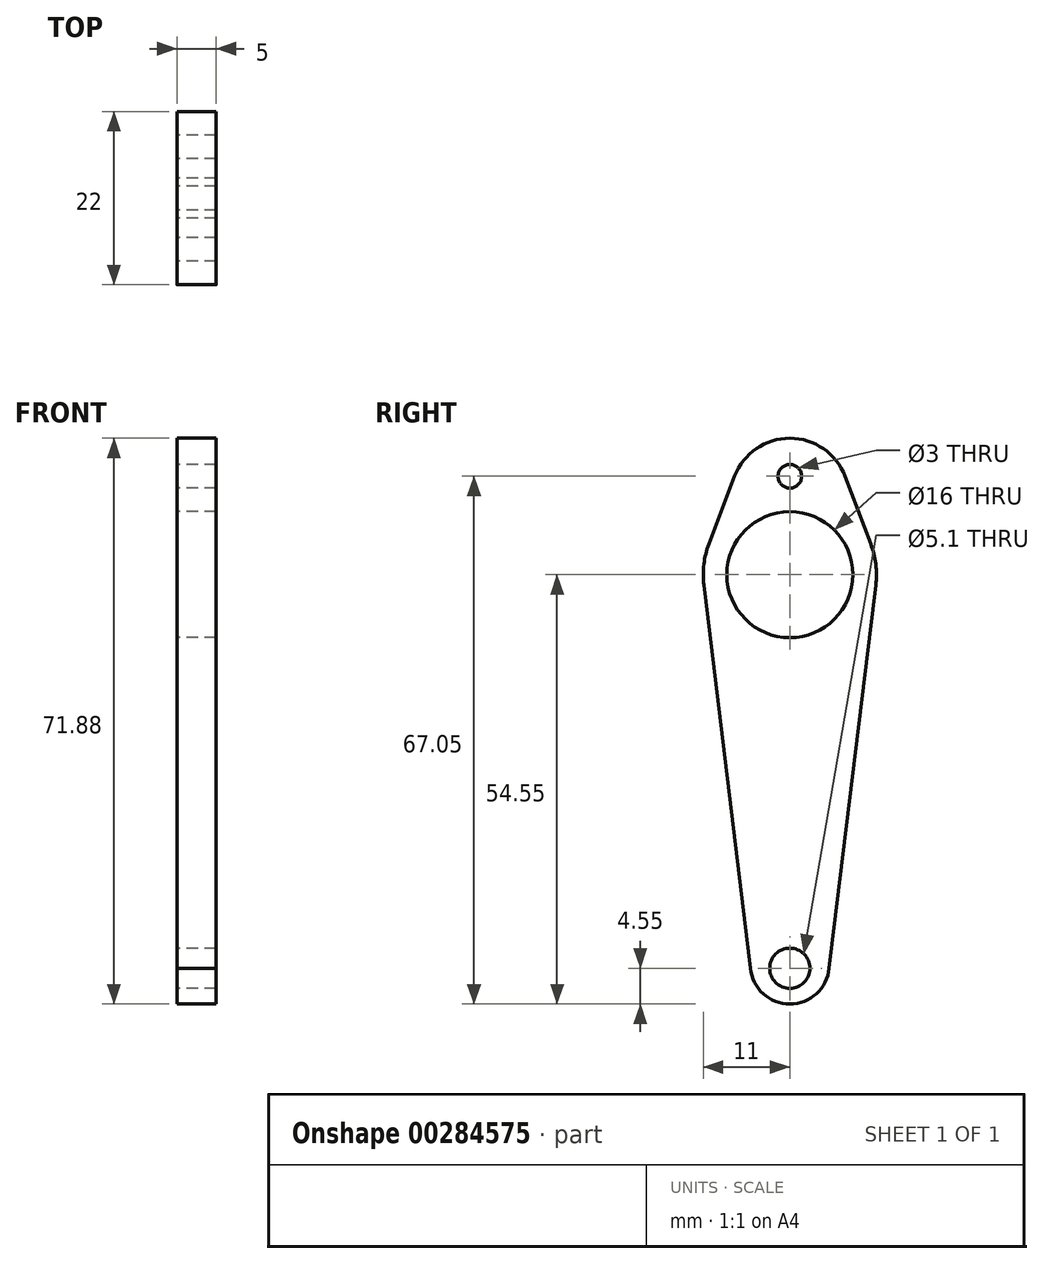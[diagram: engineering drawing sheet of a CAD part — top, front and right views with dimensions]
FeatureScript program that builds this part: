
annotation { "Feature Type Name" : "Feature", "Feature Type Description" : "" }
export const myFeature = defineFeature(function(context is Context, id is Id, definition is map)
    precondition{}
    {
        {
            var Q0;
            Q0=qCreatedBy(makeId("Right.planeOp"),FACE);
            var sketch = newSketch(context, id + "F0", { "sketchPlane" : qUnion([Q0])});
            skLineSegment(sketch, "E0", {"start": v(0, 0) * mm, "end": v(0, 12.5) * mm, "construction": true});
            skCircle(sketch, "E1", {"center": v(0, 12.5) * mm, "radius": 1.5 * mm});
            skCircle(sketch, "E2", {"center": v(0, 0) * mm, "radius": 8 * mm});
            skCircle(sketch, "E3", {"center": v(0, -50) * mm, "radius": 2.55 * mm});
            skLineSegment(sketch, "E4", {"start": v(0, 12.5) * mm, "end": v(7, 12.5) * mm, "construction": true});
            skLineSegment(sketch, "E5", {"start": v(0, 12.5) * mm, "end": v(-7, 12.5) * mm, "construction": true});
            skArc(sketch, "E6", {"start": v(7, 12.5) * mm, "mid": v(0, 17.33) * mm, "end": v(-7, 12.5) * mm});
            skLineSegment(sketch, "E7", {"start": v(-5, -50) * mm, "end": v(5, -50) * mm, "construction": true});
            skArc(sketch, "E8", {"start": v(-10.28, 3.92) * mm, "mid": v(-10.92, 1.33) * mm, "end": v(-10.92, -1.33) * mm});
            skLineSegment(sketch, "E9", {"start": v(-7, 12.5) * mm, "end": v(-10.28, 3.92) * mm});
            skLineSegment(sketch, "E10", {"start": v(7, 12.5) * mm, "end": v(10.28, 3.92) * mm});
            skLineSegment(sketch, "E11", {"start": v(-5, -50) * mm, "end": v(-10.92, -1.33) * mm});
            skLineSegment(sketch, "E12", {"start": v(5, -50) * mm, "end": v(10.92, -1.33) * mm});
            skArc(sketch, "E13.trimOffspring", {"start": v(10.92, -1.33) * mm, "mid": v(10.92, 1.33) * mm, "end": v(10.28, 3.92) * mm});
            skArc(sketch, "E14", {"start": v(-5, -50) * mm, "mid": v(0, -54.55) * mm, "end": v(5, -50) * mm});
            skSolve(sketch);
        }
        {
            var Q0;
            Q0=qSketchRegion(id+"F0",true);
            extrude(context, id + "F1", {"entities" : qUnion([Q0]), "depth" : 5 * mm});
        }
    });
